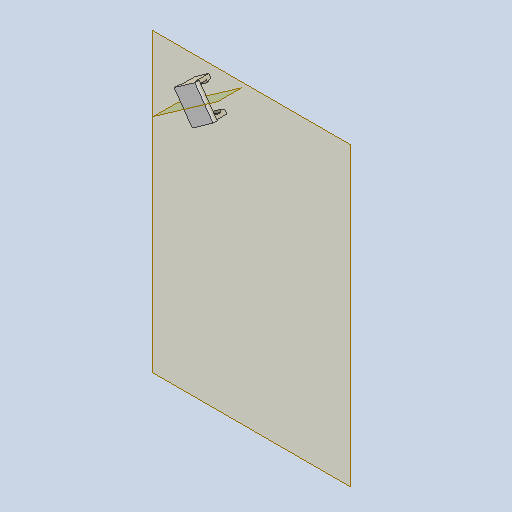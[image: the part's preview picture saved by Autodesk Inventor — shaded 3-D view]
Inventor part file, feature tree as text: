
AUTODESK INVENTOR PART (.ipt)
format: ipt  version: 2022 (Build 260153000, 153)  size: 186,880 bytes
history: native  units: mm
features: reference x6, extrude x3, sketch x3, other x3, plane x2, chamfer x1, mirror x1, projected_geometry x1
ambient origin geometry x8: Origin, YZ Plane, XZ Plane, XY Plane, X Axis, Y Axis, Z Axis, Center Point
bodies: Volumenkörper1 (feature_tree)
feature tree (20):
  plane  "Arbeitsebene1"
  extrude  "Extrusion1"  Depth=15.0mm
  extrude  "Extrusion2"  Depth=2.0mm
  chamfer  "Fase1"  Distance=2.0mm
  plane  "Arbeitsebene2"
  mirror  "Spiegeln1"
  extrude  "Extrusion3"  TaperAngle=0.0deg  [1 undecoded]
  sketch  "Skizze1"  dims[d0=21.816616mm d1=15.0mm]
  reference  "Referenz1"
  reference  "Referenz2"
  reference  "Referenz3"
  reference  "Referenz4"
  reference  "Referenz5"
  sketch  "Skizze2"  dims[d2=12.0mm d3=9.0mm d4=2.0mm d5=0.0mm]
  projected_geometry  "Projizierte Kontur1"
  reference  "Referenz6"
  sketch  "Skizze3"  dims[d6=1.5mm d7=0.0mm d8=1.0mm d9=0.3mm d10=2.0mm d11=2.0mm d12=0.0mm d13=2.0mm d14=2.0mm d15=45.0deg d16=7.9mm d17=0.0mm d18=0.0mm]
  other  "Omniscope_new_v0.iam"
  other  "OV_Camera:1"
  other  "Omniscope_mid_level_v0:1"
note: 1 required parameter value undecoded (feature->parameter linkage not recoverable at this tier; creation-order binding heuristic only, values carry confidence <= 0.55)
